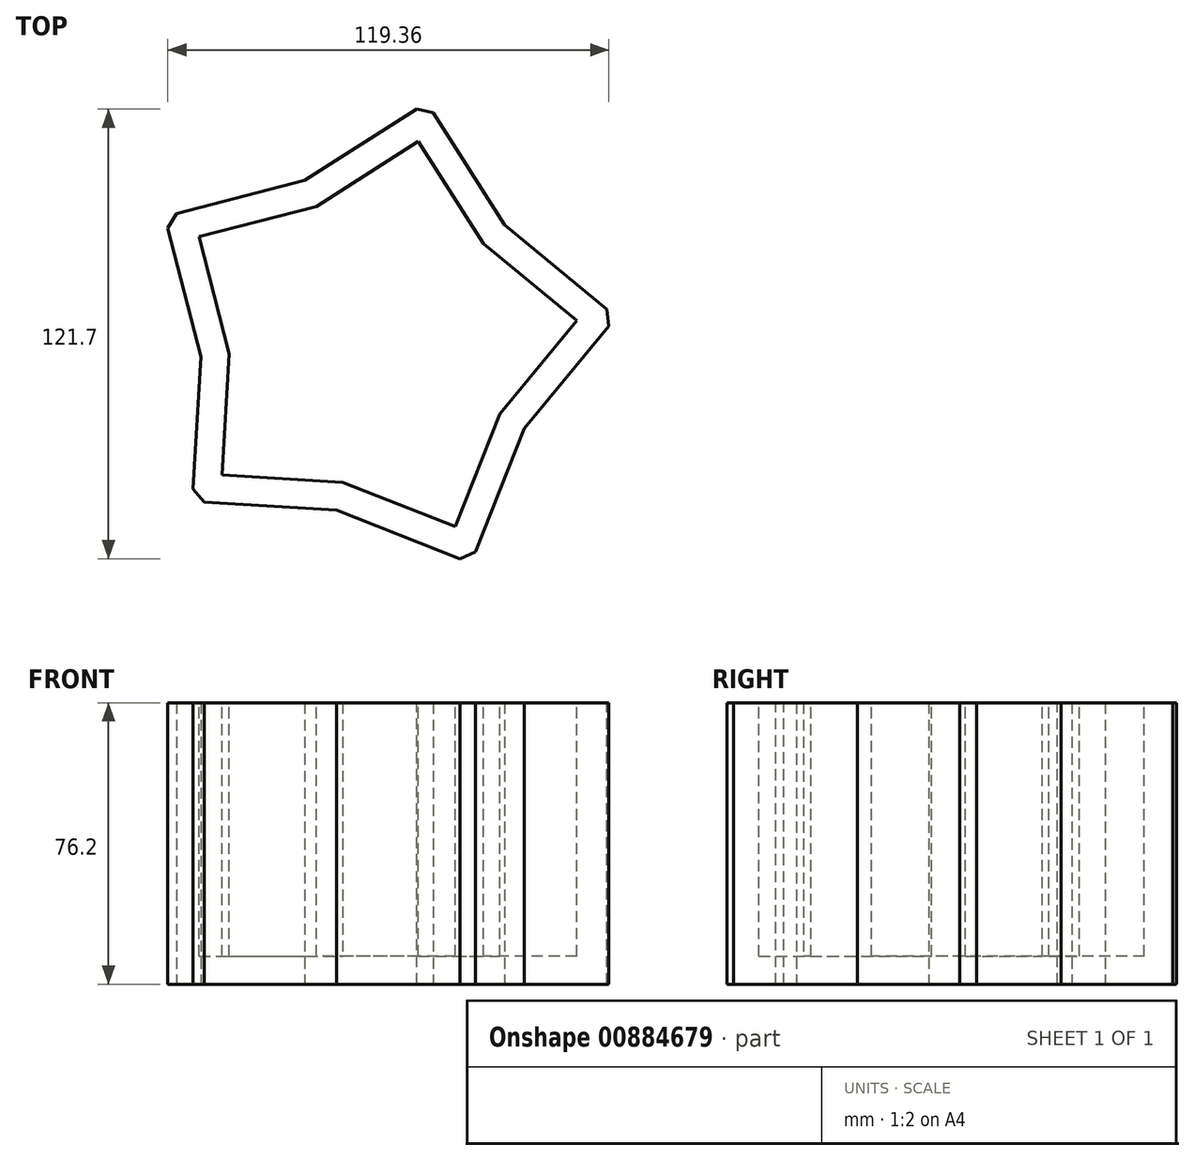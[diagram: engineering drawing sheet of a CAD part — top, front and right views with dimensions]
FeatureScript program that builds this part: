
annotation { "Feature Type Name" : "Feature", "Feature Type Description" : "" }
export const myFeature = defineFeature(function(context is Context, id is Id, definition is map)
    precondition{}
    {
        {
            var Q0;
            Q0=qCreatedBy(makeId("Top.planeOp"),FACE);
            var sketch = newSketch(context, id + "F0", { "sketchPlane" : qUnion([Q0])});
            skCircle(sketch, "E0.cCircle", {"center": v(0, 0) * mm, "radius": 38.13 * mm, "construction": true});
            skLineSegment(sketch, "E0.0", {"start": v(-46.91, -4.51) * mm, "end": v(-18.79, 43.22) * mm});
            skLineSegment(sketch, "E0.1", {"start": v(-18.79, 43.22) * mm, "end": v(35.3, 31.22) * mm});
            skLineSegment(sketch, "E0.2", {"start": v(35.3, 31.22) * mm, "end": v(40.6, -23.92) * mm});
            skLineSegment(sketch, "E0.3", {"start": v(40.6, -23.92) * mm, "end": v(-10.2, -46) * mm});
            skLineSegment(sketch, "E0.4", {"start": v(-10.2, -46) * mm, "end": v(-46.91, -4.51) * mm});
            skPoint(sketch, "E0.0.midPoint", {"position": v(-32.85, 19.36) * mm});
            skSolve(sketch);
        }
        {
            var Q0;
            Q0=makeQuery(id+"F0.imprint","IMPRINT",FACE,{"disambiguationData":[TD([[makeQuery(id+"F0.imprint","IMPRINT",EDGE,{"derivedFrom":sQuery(id+"F0.wireOp",EDGE,"E0.0")}),-1.0]])]});
            extrude(context, id + "F1", {"entities" : qUnion([Q0]), "depth" : 76.2 * mm, "offsetDistance" : 25.4 * mm});
        }
        {
            var Q0;
            Q0=makeQuery(id+"F1.opExtrude","SWEPT_FACE",FACE,{"disambiguationData":[OSD([sQuery(id+"F0.wireOp",EDGE,"E0.3")])]});
            extrude(context, id + "F2", {"entities" : qUnion([Q0]), "operationType" : NewBodyOperationType.ADD, "depth" : 25.4 * mm, "offsetDistance" : 25.4 * mm});
        }
        {
            var Q0;
            Q0=makeQuery(id+"F1.opExtrude","SWEPT_FACE",FACE,{"disambiguationData":[OSD([sQuery(id+"F0.wireOp",EDGE,"E0.2")])]});
            extrude(context, id + "F3", {"entities" : qUnion([Q0]), "operationType" : NewBodyOperationType.ADD, "depth" : 25.4 * mm, "offsetDistance" : 25.4 * mm});
        }
        {
            var Q0;
            Q0=makeQuery(id+"F1.opExtrude","SWEPT_FACE",FACE,{"disambiguationData":[OSD([sQuery(id+"F0.wireOp",EDGE,"E0.1")])]});
            extrude(context, id + "F4", {"entities" : qUnion([Q0]), "operationType" : NewBodyOperationType.ADD, "depth" : 25.4 * mm, "offsetDistance" : 25.4 * mm});
        }
        {
            var Q0;
            Q0=makeQuery(id+"F1.opExtrude","SWEPT_FACE",FACE,{"disambiguationData":[OSD([sQuery(id+"F0.wireOp",EDGE,"E0.0")])]});
            extrude(context, id + "F5", {"entities" : qUnion([Q0]), "operationType" : NewBodyOperationType.ADD, "depth" : 25.4 * mm, "offsetDistance" : 25.4 * mm});
        }
        {
            var Q0;
            Q0=makeQuery(id+"F1.opExtrude","SWEPT_FACE",FACE,{"disambiguationData":[OSD([sQuery(id+"F0.wireOp",EDGE,"E0.4")])]});
            extrude(context, id + "F6", {"entities" : qUnion([Q0]), "operationType" : NewBodyOperationType.ADD, "depth" : 25.4 * mm, "offsetDistance" : 25.4 * mm});
        }
        {
            var Q0;
            Q0=makeQuery(id+"F2.opExtrude","CAP_EDGE",EDGE,{"disambiguationData":[OSD([sQuery(id+"F0.wireOp",EDGE,"E0.2"),sQuery(id+"F0.wireOp",EDGE,"E0.3")])],"isStart":false});
            var Q1;
            Q1=makeQuery(id+"F2.opExtrude","CAP_EDGE",EDGE,{"disambiguationData":[OSD([sQuery(id+"F0.wireOp",EDGE,"E0.3"),sQuery(id+"F0.wireOp",EDGE,"E0.4")])],"isStart":false});
            var Q2;
            Q2=makeQuery(id+"F3.opExtrude","CAP_EDGE",EDGE,{"disambiguationData":[OSD([sQuery(id+"F0.wireOp",EDGE,"E0.2"),sQuery(id+"F0.wireOp",EDGE,"E0.3")])],"isStart":false});
            var Q3;
            Q3=makeQuery(id+"F3.opExtrude","CAP_EDGE",EDGE,{"disambiguationData":[OSD([sQuery(id+"F0.wireOp",EDGE,"E0.1"),sQuery(id+"F0.wireOp",EDGE,"E0.2")])],"isStart":false});
            var Q4;
            Q4=makeQuery(id+"F6.opExtrude","CAP_EDGE",EDGE,{"disambiguationData":[OSD([sQuery(id+"F0.wireOp",EDGE,"E0.0"),sQuery(id+"F0.wireOp",EDGE,"E0.4")])],"isStart":false});
            var Q5;
            Q5=makeQuery(id+"F6.opExtrude","CAP_EDGE",EDGE,{"disambiguationData":[OSD([sQuery(id+"F0.wireOp",EDGE,"E0.3"),sQuery(id+"F0.wireOp",EDGE,"E0.4")])],"isStart":false});
            var Q6;
            Q6=makeQuery(id+"F4.opExtrude","CAP_EDGE",EDGE,{"disambiguationData":[OSD([sQuery(id+"F0.wireOp",EDGE,"E0.0"),sQuery(id+"F0.wireOp",EDGE,"E0.1")])],"isStart":false});
            var Q7;
            Q7=makeQuery(id+"F4.opExtrude","CAP_EDGE",EDGE,{"disambiguationData":[OSD([sQuery(id+"F0.wireOp",EDGE,"E0.1"),sQuery(id+"F0.wireOp",EDGE,"E0.2")])],"isStart":false});
            var Q8;
            Q8=makeQuery(id+"F5.opExtrude","CAP_EDGE",EDGE,{"disambiguationData":[OSD([sQuery(id+"F0.wireOp",EDGE,"E0.0"),sQuery(id+"F0.wireOp",EDGE,"E0.1")])],"isStart":false});
            var Q9;
            Q9=makeQuery(id+"F5.opExtrude","CAP_EDGE",EDGE,{"disambiguationData":[OSD([sQuery(id+"F0.wireOp",EDGE,"E0.0"),sQuery(id+"F0.wireOp",EDGE,"E0.4")])],"isStart":false});
            chamfer(context, id + "F7", {"entities" : qUnion([Q0, Q1, Q2, Q3, Q4, Q5, Q6, Q7, Q8, Q9]), "width" : 25.4 * mm, "tangentPropagation" : true});
        }
        {
            var Q0;
            {var subQ0=sQuery(id+"F0.wireOp",EDGE,"E0.4");var subQ1=sQuery(id+"F0.wireOp",EDGE,"E0.0");var subQ2=sQuery(id+"F0.wireOp",EDGE,"E0.1");var subQ3=sQuery(id+"F0.wireOp",EDGE,"E0.2");var subQ4=sQuery(id+"F0.wireOp",EDGE,"E0.3");Q0=makeQuery(id+"F6.boolean.opBoolean","MERGE",FACE,{"derivedFrom":[makeQuery(id+"F5.boolean.opBoolean","MERGE",FACE,{"derivedFrom":[makeQuery(id+"F4.boolean.opBoolean","MERGE",FACE,{"derivedFrom":[makeQuery(id+"F3.boolean.opBoolean","MERGE",FACE,{"derivedFrom":[makeQuery(id+"F2.boolean.opBoolean","MERGE",FACE,{"derivedFrom":[makeQuery(id+"F1.opExtrude","CAP_FACE",FACE,{"disambiguationData":[OSD([subQ1,subQ2,subQ3,subQ4,subQ0])],"isStart":false}),makeQuery(id+"F2.opExtrude","SWEPT_FACE",FACE,{"disambiguationData":[OSD([subQ4]),TDD([makeQuery(id+"F1.opExtrude","CAP_EDGE",EDGE,{"disambiguationData":[OSD([subQ4])],"isStart":false})])]})]}),makeQuery(id+"F3.opExtrude","SWEPT_FACE",FACE,{"disambiguationData":[OSD([subQ3]),TDD([makeQuery(id+"F1.opExtrude","CAP_EDGE",EDGE,{"disambiguationData":[OSD([subQ3])],"isStart":false})])]})]}),makeQuery(id+"F4.opExtrude","SWEPT_FACE",FACE,{"disambiguationData":[OSD([subQ2]),TDD([makeQuery(id+"F1.opExtrude","CAP_EDGE",EDGE,{"disambiguationData":[OSD([subQ2])],"isStart":false})])]})]}),makeQuery(id+"F5.opExtrude","SWEPT_FACE",FACE,{"disambiguationData":[OSD([subQ1]),TDD([makeQuery(id+"F1.opExtrude","CAP_EDGE",EDGE,{"disambiguationData":[OSD([subQ1])],"isStart":false})])]})]}),makeQuery(id+"F6.opExtrude","SWEPT_FACE",FACE,{"disambiguationData":[OSD([subQ0]),TDD([makeQuery(id+"F1.opExtrude","CAP_EDGE",EDGE,{"disambiguationData":[OSD([subQ0])],"isStart":false})])]})]});}
            shell(context, id + "F8", {"entities" : qUnion([Q0]), "thickness" : 7.62 * mm});
        }
    });
